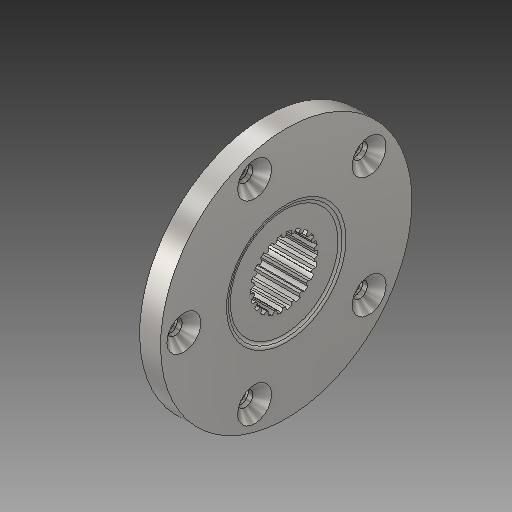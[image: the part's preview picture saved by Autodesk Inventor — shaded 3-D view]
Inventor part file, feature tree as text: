
AUTODESK INVENTOR PART (.ipt)
format: ipt  version: 2019 (Build 230136000, 136)  size: 359,936 bytes
history: native  units: mm
features: extrude x4, sketch x2, hole x2, fillet x2, pattern_circular x1, chamfer x1
ambient origin geometry x8: Origin, YZ Plane, XZ Plane, XY Plane, X Axis, Y Axis, Z Axis, Center Point
bodies: Solid1 (feature_tree)
feature tree (12):
  sketch  "Sketch1"  dims[d1=9.0mm d2=0.0mm d5=46.0mm]
  extrude  "Extrusion1"  Depth=9.0mm
  extrude  "Extrusion2"  Depth=17.0mm TaperAngle=0.0deg
  extrude  "Extrusion3"  Depth=10.0mm
  hole  "Hole1"  [1 undecoded]
  fillet  "Fillet1"  Radius=2.0mm
  fillet  "Fillet2"  Radius=17.0mm
  extrude  "Extrusion4"  Depth=2.0mm TaperAngle=360.0deg
  hole  "Hole2"  [1 undecoded]
  pattern_circular  "Circular Pattern1"  [2 undecoded]
  chamfer  "Chamfer1"  Distance=108.0mm
  sketch  "Sketch2"  dims[d6=17.0mm d7=0.0mm d8=17.0mm d9=0.0mm d10=10.0mm d11=10.0mm d12=48.0mm d13=6.0mm d14=4.0mm d15=2.0mm d16=90.0deg d17=0.9mm d18=0.0mm d19=2.0mm d20=2.0mm d21=17.0mm d22=0.0mm d49=10.0mm d50=10.0mm d25=6.6mm d26=6.0mm d27=12.0mm d28=3.0mm d29=90.0deg d30=0.9mm d31=0.0mm d32=50.0mm d33=360.0deg d35=4.0mm d36=2.0mm d37=45.0deg d39=220.0mm d40=29.0mm d41=1.0mm d42=13.0mm d43=19.896753mm d44=19.896753mm d45=360.0deg d46=25.0mm d47=43.0mm d48=108.0mm]
note: 4 required parameter values undecoded (feature->parameter linkage not recoverable at this tier; creation-order binding heuristic only, values carry confidence <= 0.55)
